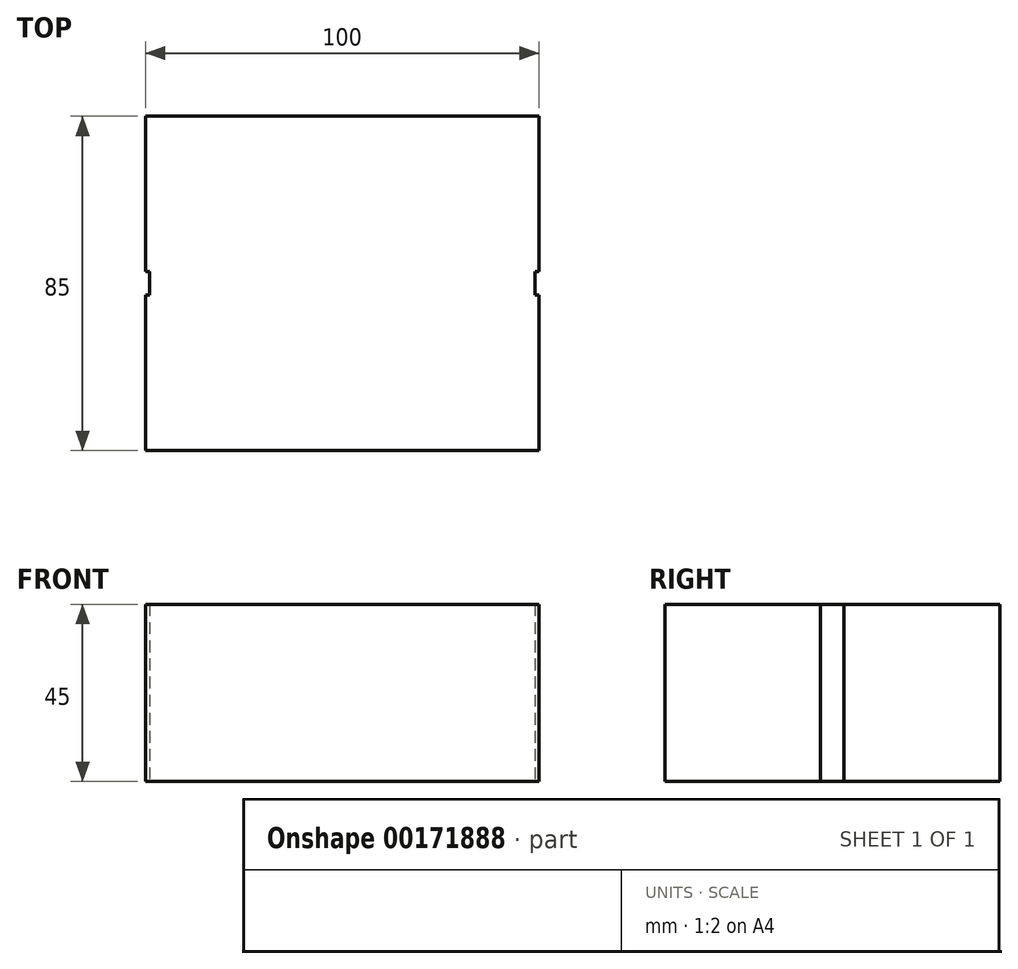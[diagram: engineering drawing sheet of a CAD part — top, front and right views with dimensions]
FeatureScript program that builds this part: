
annotation { "Feature Type Name" : "Feature", "Feature Type Description" : "" }
export const myFeature = defineFeature(function(context is Context, id is Id, definition is map)
    precondition{}
    {
        {
            var Q0;
            Q0=qCreatedBy(makeId("Top.planeOp"),FACE);
            var sketch = newSketch(context, id + "F0", { "sketchPlane" : qUnion([Q0])});
            skLineSegment(sketch, "E0.bottom", {"start": v(50, -42.5) * mm, "end": v(-50, -42.5) * mm});
            skLineSegment(sketch, "E0.top", {"start": v(50, 42.5) * mm, "end": v(-50, 42.5) * mm});
            skLineSegment(sketch, "E0.left", {"start": v(50, -42.5) * mm, "end": v(50, 42.5) * mm});
            skLineSegment(sketch, "E0.right", {"start": v(-50, -42.5) * mm, "end": v(-50, 42.5) * mm});
            skPoint(sketch, "E0.middle", {"position": v(0, 0) * mm});
            skLineSegment(sketch, "E1.bottom", {"start": v(50, 3) * mm, "end": v(49, 3) * mm});
            skLineSegment(sketch, "E1.top", {"start": v(50, -3) * mm, "end": v(49, -3) * mm});
            skLineSegment(sketch, "E1.left", {"start": v(50, 3) * mm, "end": v(50, -3) * mm});
            skLineSegment(sketch, "E1.right", {"start": v(49, 3) * mm, "end": v(49, -3) * mm});
            skLineSegment(sketch, "E2.MirrorCS", {"start": v(-49, 3) * mm, "end": v(-49, -3) * mm});
            skLineSegment(sketch, "E3.MirrorCS", {"start": v(-50, 3) * mm, "end": v(-49, 3) * mm});
            skLineSegment(sketch, "E4.MirrorCS", {"start": v(-50, 3) * mm, "end": v(-50, -3) * mm});
            skLineSegment(sketch, "E5.MirrorCS", {"start": v(-50, -3) * mm, "end": v(-49, -3) * mm});
            skSolve(sketch);
        }
        {
            var Q0;
            {var subQ1=sQuery(id+"F0.wireOp",EDGE,"E0.bottom");Q0=makeQuery(id+"F0.imprint","IMPRINT",FACE,{"disambiguationData":[TD([[makeQuery(id+"F0.imprint","IMPRINT",EDGE,{"derivedFrom":subQ1}),-1.0]])]});}
            extrude(context, id + "F1", {"entities" : qUnion([Q0]), "depth" : 45 * mm});
        }
    });
